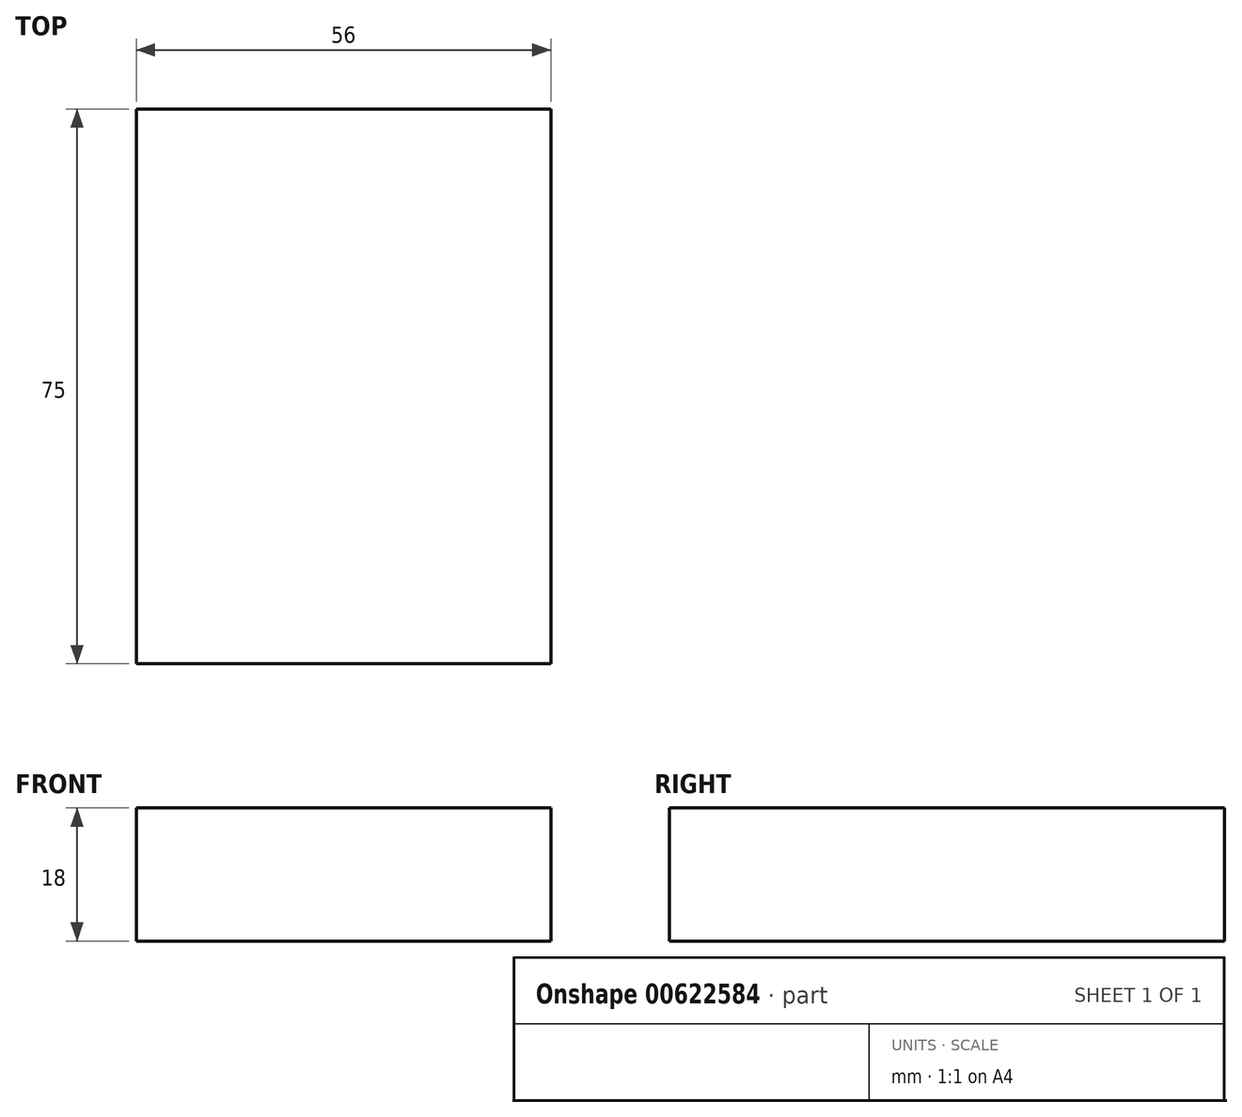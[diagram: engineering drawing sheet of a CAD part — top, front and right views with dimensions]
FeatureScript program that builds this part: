
annotation { "Feature Type Name" : "Feature", "Feature Type Description" : "" }
export const myFeature = defineFeature(function(context is Context, id is Id, definition is map)
    precondition{}
    {
        {
            var Q0;
            Q0=qCreatedBy(makeId("Top.planeOp"),FACE);
            var sketch = newSketch(context, id + "F0", { "sketchPlane" : qUnion([Q0])});
            skLineSegment(sketch, "E0.bottom", {"start": v(28, -37.5) * mm, "end": v(-28, -37.5) * mm});
            skLineSegment(sketch, "E0.top", {"start": v(28, 37.5) * mm, "end": v(-28, 37.5) * mm});
            skLineSegment(sketch, "E0.left", {"start": v(28, -37.5) * mm, "end": v(28, 37.5) * mm});
            skLineSegment(sketch, "E0.right", {"start": v(-28, -37.5) * mm, "end": v(-28, 37.5) * mm});
            skPoint(sketch, "E0.middle", {"position": v(0, 0) * mm});
            skSolve(sketch);
        }
        {
            var Q0;
            Q0 = qSketchRegion(id + "F0", true);
            extrude(context, id + "F1", {"entities" : qUnion([Q0]), "depth" : 18 * mm, "offsetDistance" : 25.4 * mm});
        }
    });
